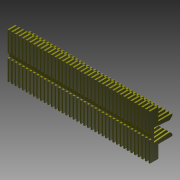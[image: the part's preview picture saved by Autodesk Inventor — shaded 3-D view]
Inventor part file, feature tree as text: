
AUTODESK INVENTOR PART (.ipt)
format: ipt  version: 2016 (Build 200138000, 138)  size: 783,872 bytes
history: native  units: mm
features: other x7, extrude x3, sketch x3
ambient origin geometry x8: Origin, YZ Plane, XZ Plane, XY Plane, X Axis, Y Axis, Z Axis, Center Point
bodies: Solid1 (feature_tree)
feature tree (13):
  extrude  "Extrusion1"  Depth=15.75mm TaperAngle=0.0deg
  extrude  "Extrusion2"  [1 undecoded]
  extrude  "Extrusion3"  [1 undecoded]
  other  "pins_to_socket_XY"
  other  "pins_to_socket_YZ"
  other  "pins_to_socket_ZX"
  other  "pins_to_socket_X"
  other  "pins_to_socket_Y"
  other  "pins_to_socket_Z"
  other  "pins_to_socket_Center"
  sketch  "Sketch_1"  dims[d0=15.75mm d1=0.0mm d2=3.0mm d3=0.0mm]
  sketch  "Sketch_3"  dims[d4=3.0mm d5=0.0mm]
  sketch  "Sketch_4"
note: 2 required parameter values undecoded (feature->parameter linkage not recoverable at this tier; creation-order binding heuristic only, values carry confidence <= 0.55)
